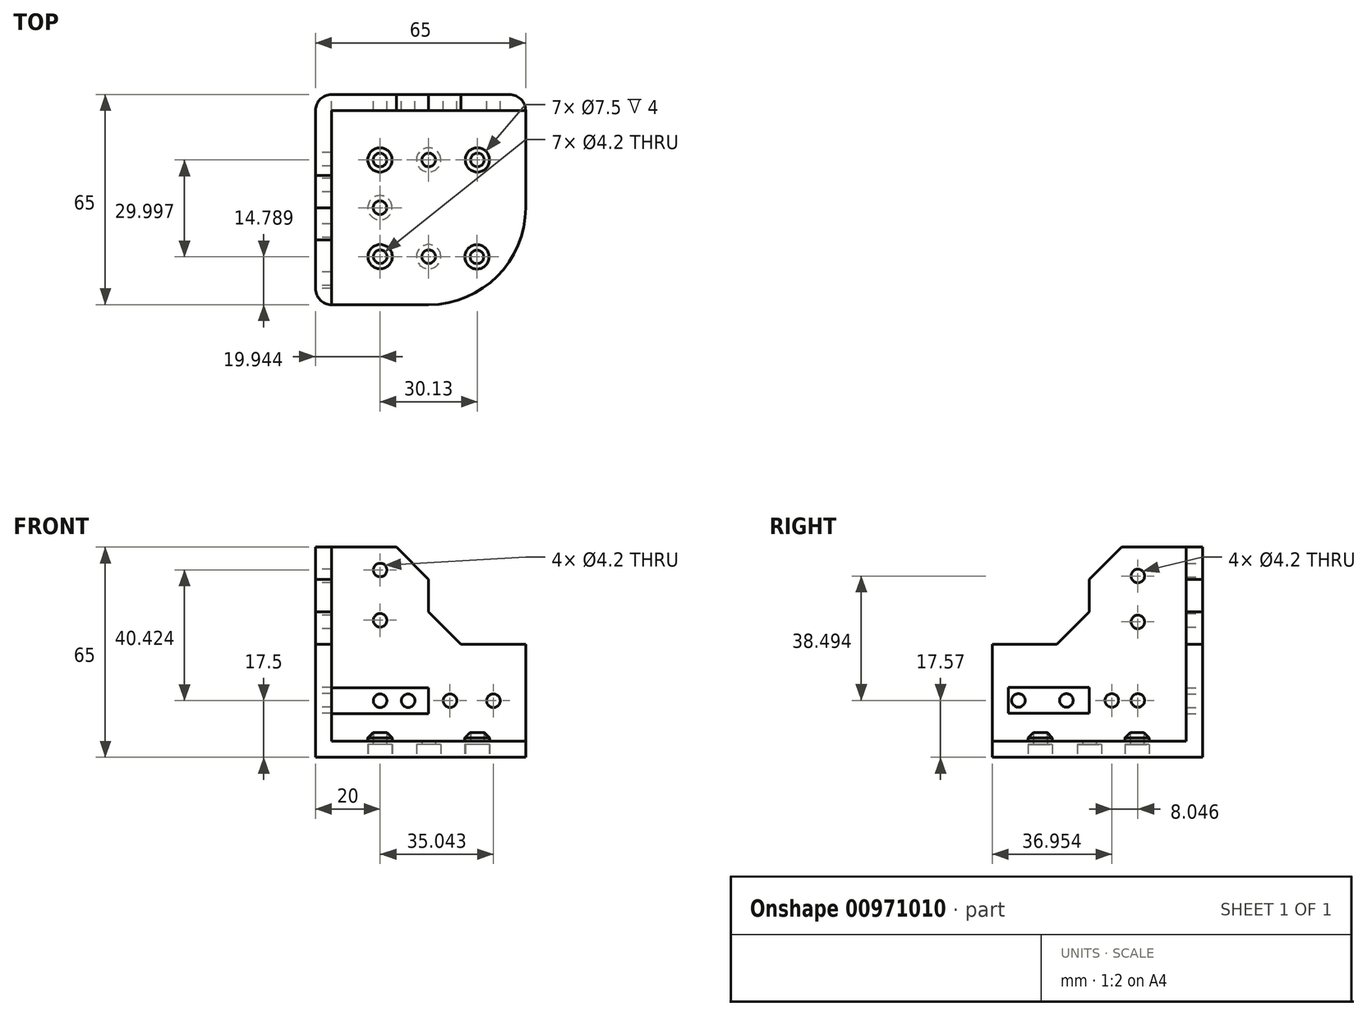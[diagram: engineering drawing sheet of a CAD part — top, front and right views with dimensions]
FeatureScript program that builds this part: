
annotation { "Feature Type Name" : "Feature", "Feature Type Description" : "" }
export const myFeature = defineFeature(function(context is Context, id is Id, definition is map)
    precondition{}
    {
        {
            var Q0;
            Q0=qCreatedBy(makeId("Top.planeOp"),FACE);
            var sketch = newSketch(context, id + "F0", { "sketchPlane" : qUnion([Q0])});
            skLineSegment(sketch, "E0.bottom", {"start": v(0, 0) * mm, "end": v(-30, 0) * mm});
            skLineSegment(sketch, "E0.top", {"start": v(0, 30) * mm, "end": v(-30, 30) * mm});
            skLineSegment(sketch, "E0.left", {"start": v(0, 0) * mm, "end": v(0, 30) * mm});
            skLineSegment(sketch, "E0.right", {"start": v(-30, 0) * mm, "end": v(-30, 30) * mm});
            skLineSegment(sketch, "E1.bottom", {"start": v(0, 30) * mm, "end": v(30, 30) * mm});
            skLineSegment(sketch, "E1.top", {"start": v(0, 0) * mm, "end": v(30, 0) * mm});
            skLineSegment(sketch, "E1.left", {"start": v(0, 30) * mm, "end": v(0, 0) * mm});
            skLineSegment(sketch, "E1.right", {"start": v(30, 30) * mm, "end": v(30, 0) * mm});
            skLineSegment(sketch, "E2.top", {"start": v(0, -30) * mm, "end": v(-30, -30) * mm});
            skLineSegment(sketch, "E2.left", {"start": v(0, 0) * mm, "end": v(0, -30) * mm});
            skLineSegment(sketch, "E2.right", {"start": v(-30, 0) * mm, "end": v(-30, -30) * mm});
            skLineSegment(sketch, "E3.bottom", {"start": v(-30, 30) * mm, "end": v(30, 30) * mm});
            skLineSegment(sketch, "E3.top", {"start": v(-30, 35) * mm, "end": v(25, 35) * mm});
            skLineSegment(sketch, "E3.left", {"start": v(-30, 30) * mm, "end": v(-30, 35) * mm});
            skLineSegment(sketch, "E3.right", {"start": v(30, 30) * mm, "end": v(30, 30) * mm});
            skLineSegment(sketch, "E4.bottom", {"start": v(-30, 30) * mm, "end": v(-35, 30) * mm});
            skLineSegment(sketch, "E4.top", {"start": v(-30, -30) * mm, "end": v(-30, -30) * mm});
            skLineSegment(sketch, "E4.left", {"start": v(-30, 30) * mm, "end": v(-30, -30) * mm});
            skLineSegment(sketch, "E4.right", {"start": v(-35, 30) * mm, "end": v(-35, -25) * mm});
            skLineSegment(sketch, "E5.top", {"start": v(-30, 35) * mm, "end": v(-30, 35) * mm});
            skLineSegment(sketch, "E5.right", {"start": v(-35, 30) * mm, "end": v(-35, 30) * mm});
            skArc(sketch, "E6", {"start": v(0, -30) * mm, "mid": v(21.21, -21.21) * mm, "end": v(30, 0) * mm});
            skPoint(sketch, "E7.visualSharp", {"position": v(-35, 35) * mm});
            skArc(sketch, "E7.filletArc", {"start": v(-30, 35) * mm, "mid": v(-33.54, 33.54) * mm, "end": v(-35, 30) * mm});
            skPoint(sketch, "E8.visualSharp", {"position": v(30, 35) * mm});
            skArc(sketch, "E8.filletArc", {"start": v(30, 30) * mm, "mid": v(28.54, 33.54) * mm, "end": v(25, 35) * mm});
            skPoint(sketch, "E9.visualSharp", {"position": v(-35, -30) * mm});
            skArc(sketch, "E9.filletArc", {"start": v(-35, -25) * mm, "mid": v(-33.54, -28.54) * mm, "end": v(-30, -30) * mm});
            skLineSegment(sketch, "E10", {"start": v(0, 30) * mm, "end": v(0, 35) * mm});
            skLineSegment(sketch, "E11", {"start": v(-30, 0) * mm, "end": v(-35, 0) * mm});
            skSolve(sketch);
        }
        {
            var Q0;
            {var subQ0=makeQuery(id+"F0.imprint","IMPRINT",EDGE,{"derivedFrom":sQuery(id+"F0.wireOp",EDGE,"E2.right")});var subQ7=sQuery(id+"F0.wireOp",EDGE,"E3.left");var subQ12=makeQuery(id+"F0.imprint","IMPRINT",EDGE,{"derivedFrom":subQ7});var subQ13=makeQuery(id+"F0.imprint","IMPRINT",EDGE,{"derivedFrom":sQuery(id+"F0.wireOp",EDGE,"E1.top")});var subQ17=makeQuery(id+"F0.imprint","IMPRINT",EDGE,{"derivedFrom":sQuery(id+"F0.wireOp",EDGE,"E1.bottom")});Q0=qUnion([makeQuery(id+"F0.imprint","IMPRINT",FACE,{"disambiguationData":[TD([[subQ12,1.0]])]}),makeQuery(id+"F0.imprint","IMPRINT",FACE,{"disambiguationData":[TD([[makeQuery(id+"F0.imprint","IMPRINT",EDGE,{"derivedFrom":sQuery(id+"F0.wireOp",EDGE,"E0.left")}),-1.0]])]}),makeQuery(id+"F0.imprint","IMPRINT",FACE,{"disambiguationData":[TD([[subQ17,1.0]])]}),makeQuery(id+"F0.imprint","IMPRINT",FACE,{"disambiguationData":[TD([[makeQuery(id+"F0.imprint","IMPRINT",EDGE,{"derivedFrom":sQuery(id+"F0.wireOp",EDGE,"E0.bottom")}),1.0]])]}),makeQuery(id+"F0.imprint","IMPRINT",FACE,{"disambiguationData":[TD([[makeQuery(id+"F0.imprint","IMPRINT",EDGE,{"derivedFrom":sQuery(id+"F0.wireOp",EDGE,"E0.right")}),1.0]])]}),makeQuery(id+"F0.imprint","IMPRINT",FACE,{"disambiguationData":[TD([[subQ13,-1.0]])]}),makeQuery(id+"F0.imprint","IMPRINT",FACE,{"disambiguationData":[TD([[makeQuery(id+"F0.imprint","IMPRINT",EDGE,{"derivedFrom":sQuery(id+"F0.wireOp",EDGE,"E0.top")}),-1.0]])]}),makeQuery(id+"F0.imprint","IMPRINT",FACE,{"disambiguationData":[TD([[subQ0,-1.0]])]})]);}
            var Q1;
            Q1=makeQuery(id+"F0.imprint","IMPRINT",FACE,{"disambiguationData":[TD([[makeQuery(id+"F0.imprint","IMPRINT",EDGE,{"derivedFrom":sQuery(id+"F0.wireOp",EDGE,"E0.bottom")}),-1.0]])]});
            extrude(context, id + "F1", {"entities" : qUnion([Q0, Q1]), "depth" : 5 * mm, "offsetDistance" : 25 * mm});
        }
        {
            var Q0;
            {Q0=qUnion([makeQuery(id+"F0.imprint","IMPRINT",FACE,{"disambiguationData":[TD([[makeQuery(id+"F0.imprint","IMPRINT",EDGE,{"derivedFrom":sQuery(id+"F0.wireOp",EDGE,"E2.right")}),-1.0]])]}),makeQuery(id+"F0.imprint","IMPRINT",FACE,{"disambiguationData":[TD([[makeQuery(id+"F0.imprint","IMPRINT",EDGE,{"derivedFrom":sQuery(id+"F0.wireOp",EDGE,"E0.right")}),1.0]])]})]);}
            var Q1;
            Q1=makeQuery(id+"F0.imprint","IMPRINT",FACE,{"disambiguationData":[TD([[makeQuery(id+"F0.imprint","IMPRINT",EDGE,{"derivedFrom":sQuery(id+"F0.wireOp",EDGE,"E3.left")}),1.0]])]});
            var Q2;
            {Q2=qUnion([makeQuery(id+"F0.imprint","IMPRINT",FACE,{"disambiguationData":[TD([[makeQuery(id+"F0.imprint","IMPRINT",EDGE,{"derivedFrom":sQuery(id+"F0.wireOp",EDGE,"E1.bottom")}),1.0]])]}),makeQuery(id+"F0.imprint","IMPRINT",FACE,{"disambiguationData":[TD([[makeQuery(id+"F0.imprint","IMPRINT",EDGE,{"derivedFrom":sQuery(id+"F0.wireOp",EDGE,"E0.top")}),-1.0]])]})]);}
            extrude(context, id + "F2", {"entities" : qUnion([Q0, Q1, Q2]), "operationType" : NewBodyOperationType.ADD, "depth" : 35 * mm, "offsetDistance" : 25 * mm});
        }
        {
            var Q0;
            Q0=makeQuery(id+"F0.imprint","IMPRINT",FACE,{"disambiguationData":[TD([[makeQuery(id+"F0.imprint","IMPRINT",EDGE,{"derivedFrom":sQuery(id+"F0.wireOp",EDGE,"E0.top")}),-1.0]])]});
            var Q1;
            Q1=makeQuery(id+"F0.imprint","IMPRINT",FACE,{"disambiguationData":[TD([[makeQuery(id+"F0.imprint","IMPRINT",EDGE,{"derivedFrom":sQuery(id+"F0.wireOp",EDGE,"E3.left")}),1.0]])]});
            var Q2;
            Q2=makeQuery(id+"F0.imprint","IMPRINT",FACE,{"disambiguationData":[TD([[makeQuery(id+"F0.imprint","IMPRINT",EDGE,{"derivedFrom":sQuery(id+"F0.wireOp",EDGE,"E0.right")}),1.0]])]});
            extrude(context, id + "F3", {"entities" : qUnion([Q0, Q1, Q2]), "operationType" : NewBodyOperationType.ADD, "depth" : 65 * mm, "offsetDistance" : 25 * mm});
        }
        {
            var Q0;
            {var subQ0=sQuery(id+"F0.wireOp",EDGE,"E3.top");Q0=makeQuery(id+"F3.boolean.opBoolean","MERGE",FACE,{"derivedFrom":[makeQuery(id+"F2.boolean.opBoolean","MERGE",FACE,{"derivedFrom":[makeQuery(id+"F1.opExtrude","SWEPT_FACE",FACE,{"disambiguationData":[OSD([subQ0])]}),makeQuery(id+"F2.opExtrude","SWEPT_FACE",FACE,{"disambiguationData":[OSD([subQ0])]})]}),makeQuery(id+"F3.opExtrude","SWEPT_FACE",FACE,{"disambiguationData":[OSD([subQ0])]})]});}
            var sketch = newSketch(context, id + "F4", { "sketchPlane" : qUnion([Q0])});
            skLineSegment(sketch, "E12.bottom", {"start": v(-25, 0) * mm, "end": v(30, 0) * mm, "construction": true});
            skLineSegment(sketch, "E12.top", {"start": v(-25, 35) * mm, "end": v(30, 35) * mm, "construction": true});
            skLineSegment(sketch, "E12.left", {"start": v(-25, 0) * mm, "end": v(-25, 35) * mm, "construction": true});
            skLineSegment(sketch, "E12.right", {"start": v(30, 0) * mm, "end": v(30, 35) * mm, "construction": true});
            skLineSegment(sketch, "E13.bottom", {"start": v(-25, 21.5) * mm, "end": v(30, 21.5) * mm});
            skLineSegment(sketch, "E13.top", {"start": v(-25, 13.5) * mm, "end": v(30, 13.5) * mm});
            skLineSegment(sketch, "E13.left", {"start": v(-25, 21.5) * mm, "end": v(-25, 13.5) * mm});
            skLineSegment(sketch, "E13.right", {"start": v(30, 21.5) * mm, "end": v(30, 13.5) * mm});
            skLineSegment(sketch, "E14", {"start": v(0, 21.5) * mm, "end": v(0, 13.5) * mm});
            skCircle(sketch, "E15", {"center": v(-20.04, 17.5) * mm, "radius": 2.1 * mm});
            skPoint(sketch, "E15.centerSnap0", {"position": v(-25, 17.5) * mm});
            skCircle(sketch, "E16", {"center": v(-6.61, 17.5) * mm, "radius": 2.1 * mm});
            skCircle(sketch, "E17.MirrorC", {"center": v(15, 17.5) * mm, "radius": 2.1 * mm});
            skCircle(sketch, "E18.MirrorC", {"center": v(6.32, 17.5) * mm, "radius": 2.1 * mm});
            skCircle(sketch, "E19", {"center": v(15, 57.92) * mm, "radius": 2.1 * mm});
            skCircle(sketch, "E20", {"center": v(15, 42.38) * mm, "radius": 2.1 * mm});
            skSolve(sketch);
        }
        {
            var Q0;
            {var subQ0=sQuery(id+"F0.wireOp",EDGE,"E4.right");Q0=makeQuery(id+"F3.boolean.opBoolean","MERGE",FACE,{"derivedFrom":[makeQuery(id+"F2.boolean.opBoolean","MERGE",FACE,{"derivedFrom":[makeQuery(id+"F1.opExtrude","SWEPT_FACE",FACE,{"disambiguationData":[OSD([subQ0])]}),makeQuery(id+"F2.opExtrude","SWEPT_FACE",FACE,{"disambiguationData":[OSD([subQ0])]})]}),makeQuery(id+"F3.opExtrude","SWEPT_FACE",FACE,{"disambiguationData":[OSD([subQ0])]})]});}
            var sketch = newSketch(context, id + "F5", { "sketchPlane" : qUnion([Q0])});
            skLineSegment(sketch, "E21.bottom", {"start": v(-35, 21.57) * mm, "end": v(25, 21.57) * mm});
            skLineSegment(sketch, "E21.top", {"start": v(-35, 13.57) * mm, "end": v(25, 13.57) * mm});
            skLineSegment(sketch, "E21.left", {"start": v(-35, 21.57) * mm, "end": v(-35, 13.57) * mm});
            skLineSegment(sketch, "E21.right", {"start": v(25, 21.57) * mm, "end": v(25, 13.57) * mm});
            skLineSegment(sketch, "E22", {"start": v(0, 21.57) * mm, "end": v(0, 13.57) * mm});
            skCircle(sketch, "E23", {"center": v(-6.95, 17.57) * mm, "radius": 2.1 * mm});
            skPoint(sketch, "E23.centerSnap0", {"position": v(-35, 17.57) * mm});
            skCircle(sketch, "E24", {"center": v(-15, 17.57) * mm, "radius": 2.1 * mm});
            skCircle(sketch, "E25.MirrorC", {"center": v(7.1, 17.57) * mm, "radius": 2.1 * mm});
            skCircle(sketch, "E26.MirrorC", {"center": v(21.94, 17.57) * mm, "radius": 2.1 * mm});
            skCircle(sketch, "E27", {"center": v(-15, 41.87) * mm, "radius": 2.1 * mm});
            skCircle(sketch, "E28", {"center": v(-15, 56.06) * mm, "radius": 2.1 * mm});
            skSolve(sketch);
        }
        {
            var Q0;
            Q0=makeQuery(id+"F4.imprint","IMPRINT",FACE,{"disambiguationData":[TD([[makeQuery(id+"F4.imprint","IMPRINT",EDGE,{"derivedFrom":sQuery(id+"F4.wireOp",EDGE,"E17.MirrorC")}),-1.0]])]});
            var Q1;
            Q1=makeQuery(id+"F4.imprint","IMPRINT",FACE,{"disambiguationData":[TD([[makeQuery(id+"F4.imprint","IMPRINT",EDGE,{"derivedFrom":sQuery(id+"F4.wireOp",EDGE,"E18.MirrorC")}),-1.0]])]});
            var Q2;
            Q2=makeQuery(id+"F4.imprint","IMPRINT",FACE,{"disambiguationData":[TD([[makeQuery(id+"F4.imprint","IMPRINT",EDGE,{"derivedFrom":sQuery(id+"F4.wireOp",EDGE,"E16")}),1.0]])]});
            var Q3;
            Q3=makeQuery(id+"F4.imprint","IMPRINT",FACE,{"disambiguationData":[TD([[makeQuery(id+"F4.imprint","IMPRINT",EDGE,{"derivedFrom":sQuery(id+"F4.wireOp",EDGE,"E15")}),1.0]])]});
            var Q4;
            Q4=makeQuery(id+"F4.imprint","IMPRINT",FACE,{"disambiguationData":[TD([[makeQuery(id+"F4.imprint","IMPRINT",EDGE,{"derivedFrom":sQuery(id+"F4.wireOp",EDGE,"E20")}),1.0]])]});
            var Q5;
            Q5=makeQuery(id+"F4.imprint","IMPRINT",FACE,{"disambiguationData":[TD([[makeQuery(id+"F4.imprint","IMPRINT",EDGE,{"derivedFrom":sQuery(id+"F4.wireOp",EDGE,"E19")}),1.0]])]});
            extrude(context, id + "F6", {"entities" : qUnion([Q0, Q1, Q2, Q3, Q4, Q5]), "operationType" : NewBodyOperationType.REMOVE, "oppositeDirection" : true, "depth" : 25 * mm, "offsetDistance" : 25 * mm});
        }
        {
            var Q0;
            Q0=makeQuery(id+"F5.imprint","IMPRINT",FACE,{"disambiguationData":[TD([[makeQuery(id+"F5.imprint","IMPRINT",EDGE,{"derivedFrom":sQuery(id+"F5.wireOp",EDGE,"E26.MirrorC")}),-1.0]])]});
            var Q1;
            Q1=makeQuery(id+"F5.imprint","IMPRINT",FACE,{"disambiguationData":[TD([[makeQuery(id+"F5.imprint","IMPRINT",EDGE,{"derivedFrom":sQuery(id+"F5.wireOp",EDGE,"E25.MirrorC")}),-1.0]])]});
            var Q2;
            Q2=makeQuery(id+"F5.imprint","IMPRINT",FACE,{"disambiguationData":[TD([[makeQuery(id+"F5.imprint","IMPRINT",EDGE,{"derivedFrom":sQuery(id+"F5.wireOp",EDGE,"E24")}),1.0]])]});
            var Q3;
            Q3=makeQuery(id+"F5.imprint","IMPRINT",FACE,{"disambiguationData":[TD([[makeQuery(id+"F5.imprint","IMPRINT",EDGE,{"derivedFrom":sQuery(id+"F5.wireOp",EDGE,"E23")}),1.0]])]});
            var Q4;
            Q4=makeQuery(id+"F5.imprint","IMPRINT",FACE,{"disambiguationData":[TD([[makeQuery(id+"F5.imprint","IMPRINT",EDGE,{"derivedFrom":sQuery(id+"F5.wireOp",EDGE,"E27")}),1.0]])]});
            var Q5;
            Q5=makeQuery(id+"F5.imprint","IMPRINT",FACE,{"disambiguationData":[TD([[makeQuery(id+"F5.imprint","IMPRINT",EDGE,{"derivedFrom":sQuery(id+"F5.wireOp",EDGE,"E28")}),1.0]])]});
            extrude(context, id + "F7", {"entities" : qUnion([Q0, Q1, Q2, Q3, Q4, Q5]), "operationType" : NewBodyOperationType.REMOVE, "oppositeDirection" : true, "depth" : 25 * mm, "offsetDistance" : 25 * mm});
        }
        {
            var Q0;
            Q0=makeQuery(id+"F0.imprint","IMPRINT",FACE,{"disambiguationData":[TD([[makeQuery(id+"F0.imprint","IMPRINT",EDGE,{"derivedFrom":sQuery(id+"F0.wireOp",EDGE,"E0.bottom")}),1.0]])]});
            var sketch = newSketch(context, id + "F8", { "sketchPlane" : qUnion([Q0])});
            skLineSegment(sketch, "E29", {"start": v(-30.14, -30.28) * mm, "end": v(30.02, 29.68) * mm, "construction": true});
            skLineSegment(sketch, "E30", {"start": v(30.02, 29.68) * mm, "end": v(-29.98, 29.68) * mm, "construction": true});
            skLineSegment(sketch, "E31", {"start": v(-29.98, 29.68) * mm, "end": v(30.02, -30.28) * mm, "construction": true});
            skLineSegment(sketch, "E32", {"start": v(30.02, -30.28) * mm, "end": v(-30.14, -30.28) * mm, "construction": true});
            skLineSegment(sketch, "E33", {"start": v(0.02, 29.68) * mm, "end": v(-29.98, 0) * mm, "construction": true});
            skLineSegment(sketch, "E34", {"start": v(-29.98, 0) * mm, "end": v(30.02, 0) * mm, "construction": true});
            skLineSegment(sketch, "E35", {"start": v(30.02, 0) * mm, "end": v(0.02, 29.68) * mm, "construction": true});
            skLineSegment(sketch, "E36", {"start": v(0, -30.28) * mm, "end": v(-29.98, 0) * mm, "construction": true});
            skLineSegment(sketch, "E37", {"start": v(0, -30.28) * mm, "end": v(30.02, 0) * mm, "construction": true});
            skCircle(sketch, "E38", {"center": v(15.07, 14.79) * mm, "radius": 2.1 * mm});
            skCircle(sketch, "E39", {"center": v(-15, -15.14) * mm, "radius": 2.1 * mm});
            skCircle(sketch, "E40", {"center": v(-15.06, 14.77) * mm, "radius": 2.1 * mm});
            skCircle(sketch, "E41", {"center": v(0, 14.77) * mm, "radius": 2.1 * mm});
            skCircle(sketch, "E42", {"center": v(-15.06, 0) * mm, "radius": 2.1 * mm});
            skCircle(sketch, "E43", {"center": v(0, -15.14) * mm, "radius": 2.1 * mm});
            skCircle(sketch, "E44", {"center": v(14.94, -15.21) * mm, "radius": 2.1 * mm});
            skCircle(sketch, "E45", {"center": v(-15.06, 14.77) * mm, "radius": 3.75 * mm});
            skCircle(sketch, "E46", {"center": v(0, 14.77) * mm, "radius": 3.75 * mm});
            skCircle(sketch, "E47", {"center": v(15.07, 14.79) * mm, "radius": 3.75 * mm});
            skCircle(sketch, "E48", {"center": v(14.94, -15.21) * mm, "radius": 3.75 * mm});
            skCircle(sketch, "E49", {"center": v(0, -15.14) * mm, "radius": 3.75 * mm});
            skCircle(sketch, "E50", {"center": v(-15, -15.14) * mm, "radius": 3.75 * mm});
            skCircle(sketch, "E51", {"center": v(-15.06, 0) * mm, "radius": 3.75 * mm});
            skSolve(sketch);
        }
        {
            var Q0;
            Q0 = qSketchRegion(id + "F8", true);
            extrude(context, id + "F9", {"entities" : qUnion([Q0]), "operationType" : NewBodyOperationType.REMOVE, "depth" : 4 * mm, "offsetDistance" : 25 * mm});
        }
        {
            var Q0;
            Q0=makeQuery(id+"F8.imprint","IMPRINT",FACE,{"disambiguationData":[TD([[makeQuery(id+"F8.imprint","IMPRINT",EDGE,{"derivedFrom":sQuery(id+"F8.wireOp",EDGE,"E39")}),1.0]])]});
            var Q1;
            {var subQ0=sQuery(id+"F8.wireOp",EDGE,"E43");var subQ1=makeQuery(id+"F0.imprint","IMPRINT",EDGE,{"derivedFrom":sQuery(id+"F0.wireOp",EDGE,"E2.left")});var subQ2=makeQuery(id+"F8.imprint","INTERSECT",VERTEX,{"disambiguationData":[OD(0.0)],"derivedFrom":[subQ1,subQ0]});Q1=makeQuery(id+"F8.imprint","IMPRINT",FACE,{"disambiguationData":[TD([[makeQuery(id+"F8.imprint","IMPRINT",EDGE,{"disambiguationData":[TD([[subQ2,-1.0]])],"derivedFrom":subQ0}),1.0]])]});}
            var Q2;
            {var subQ0=sQuery(id+"F8.wireOp",EDGE,"E43");var subQ1=makeQuery(id+"F0.imprint","IMPRINT",EDGE,{"derivedFrom":sQuery(id+"F0.wireOp",EDGE,"E2.left")});var subQ2=makeQuery(id+"F8.imprint","INTERSECT",VERTEX,{"disambiguationData":[OD(0.0)],"derivedFrom":[subQ1,subQ0]});Q2=makeQuery(id+"F8.imprint","IMPRINT",FACE,{"disambiguationData":[TD([[makeQuery(id+"F8.imprint","IMPRINT",EDGE,{"disambiguationData":[TD([[subQ2,1.0]])],"derivedFrom":subQ0}),1.0]])]});}
            var Q3;
            Q3=makeQuery(id+"F8.imprint","IMPRINT",FACE,{"disambiguationData":[TD([[makeQuery(id+"F8.imprint","IMPRINT",EDGE,{"derivedFrom":sQuery(id+"F8.wireOp",EDGE,"E44")}),1.0]])]});
            var Q4;
            Q4=makeQuery(id+"F8.imprint","IMPRINT",FACE,{"disambiguationData":[TD([[makeQuery(id+"F8.imprint","IMPRINT",EDGE,{"derivedFrom":sQuery(id+"F8.wireOp",EDGE,"E38")}),1.0]])]});
            var Q5;
            Q5=makeQuery(id+"F8.imprint","IMPRINT",FACE,{"disambiguationData":[TD([[makeQuery(id+"F8.imprint","IMPRINT",EDGE,{"derivedFrom":sQuery(id+"F8.wireOp",EDGE,"E41")}),1.0]])]});
            var Q6;
            Q6=makeQuery(id+"F8.imprint","IMPRINT",FACE,{"disambiguationData":[TD([[makeQuery(id+"F8.imprint","IMPRINT",EDGE,{"derivedFrom":sQuery(id+"F8.wireOp",EDGE,"E40")}),1.0]])]});
            var Q7;
            {var subQ0=sQuery(id+"F8.wireOp",EDGE,"E42");var subQ1=makeQuery(id+"F0.imprint","IMPRINT",EDGE,{"derivedFrom":sQuery(id+"F0.wireOp",EDGE,"E0.bottom")});var subQ2=makeQuery(id+"F8.imprint","INTERSECT",VERTEX,{"disambiguationData":[OD(0.0)],"derivedFrom":[subQ1,subQ0]});Q7=makeQuery(id+"F8.imprint","IMPRINT",FACE,{"disambiguationData":[TD([[makeQuery(id+"F8.imprint","IMPRINT",EDGE,{"disambiguationData":[TD([[subQ2,-1.0]])],"derivedFrom":subQ0}),1.0]])]});}
            var Q8;
            {var subQ0=sQuery(id+"F8.wireOp",EDGE,"E42");var subQ1=makeQuery(id+"F0.imprint","IMPRINT",EDGE,{"derivedFrom":sQuery(id+"F0.wireOp",EDGE,"E0.bottom")});var subQ2=makeQuery(id+"F8.imprint","INTERSECT",VERTEX,{"disambiguationData":[OD(0.0)],"derivedFrom":[subQ1,subQ0]});Q8=makeQuery(id+"F8.imprint","IMPRINT",FACE,{"disambiguationData":[TD([[makeQuery(id+"F8.imprint","IMPRINT",EDGE,{"disambiguationData":[TD([[subQ2,1.0]])],"derivedFrom":subQ0}),1.0]])]});}
            extrude(context, id + "F10", {"entities" : qUnion([Q0, Q1, Q2, Q3, Q4, Q5, Q6, Q7, Q8]), "operationType" : NewBodyOperationType.REMOVE, "depth" : 25 * mm, "offsetDistance" : 25 * mm});
        }
        {
            var Q0;
            Q0=makeQuery(id+"F8.imprint","IMPRINT",FACE,{"disambiguationData":[TD([[makeQuery(id+"F8.imprint","IMPRINT",EDGE,{"derivedFrom":sQuery(id+"F8.wireOp",EDGE,"E39")}),-1.0]])]});
            var Q1;
            Q1=makeQuery(id+"F8.imprint","IMPRINT",FACE,{"disambiguationData":[TD([[makeQuery(id+"F8.imprint","IMPRINT",EDGE,{"derivedFrom":sQuery(id+"F8.wireOp",EDGE,"E44")}),-1.0]])]});
            var Q2;
            Q2=makeQuery(id+"F8.imprint","IMPRINT",FACE,{"disambiguationData":[TD([[makeQuery(id+"F8.imprint","IMPRINT",EDGE,{"derivedFrom":sQuery(id+"F8.wireOp",EDGE,"E40")}),-1.0]])]});
            var Q3;
            Q3=makeQuery(id+"F8.imprint","IMPRINT",FACE,{"disambiguationData":[TD([[makeQuery(id+"F8.imprint","IMPRINT",EDGE,{"derivedFrom":sQuery(id+"F8.wireOp",EDGE,"E38")}),-1.0]])]});
            extrude(context, id + "F11", {"entities" : qUnion([Q0, Q1, Q2, Q3]), "operationType" : NewBodyOperationType.ADD, "depth" : 8 * mm, "offsetDistance" : 25 * mm, "hasSecondDirection" : true, "secondDirectionOppositeDirection" : false, "secondDirectionDepth" : 4 * mm});
        }
        {
            var Q0;
            Q0=makeQuery(id+"F11.opExtrude","CAP_EDGE",EDGE,{"disambiguationData":[OSD([sQuery(id+"F8.wireOp",EDGE,"E45")])],"isStart":false});
            var Q1;
            Q1=makeQuery(id+"F11.opExtrude","CAP_EDGE",EDGE,{"disambiguationData":[OSD([sQuery(id+"F8.wireOp",EDGE,"E46")])],"isStart":false});
            var Q2;
            Q2=makeQuery(id+"F11.opExtrude","CAP_EDGE",EDGE,{"disambiguationData":[OSD([sQuery(id+"F8.wireOp",EDGE,"E47")])],"isStart":false});
            var Q3;
            Q3=makeQuery(id+"F11.opExtrude","CAP_EDGE",EDGE,{"disambiguationData":[OSD([sQuery(id+"F8.wireOp",EDGE,"E48")])],"isStart":false});
            var Q4;
            Q4=makeQuery(id+"F11.opExtrude","CAP_EDGE",EDGE,{"disambiguationData":[OSD([sQuery(id+"F8.wireOp",EDGE,"E49")])],"isStart":false});
            var Q5;
            Q5=makeQuery(id+"F11.opExtrude","CAP_EDGE",EDGE,{"disambiguationData":[OSD([sQuery(id+"F8.wireOp",EDGE,"E50")])],"isStart":false});
            chamfer(context, id + "F12", {"entities" : qUnion([Q0, Q1, Q2, Q3, Q4, Q5]), "width" : 2 * mm, "tangentPropagation" : true});
        }
        {
            var Q0;
            Q0=makeQuery(id+"F3.opExtrude","CAP_EDGE",EDGE,{"disambiguationData":[OSD([sQuery(id+"F0.wireOp",EDGE,"E11")])],"isStart":false});
            var Q1;
            Q1=makeQuery(id+"F3.opExtrude","CAP_EDGE",EDGE,{"disambiguationData":[OSD([sQuery(id+"F0.wireOp",EDGE,"E10")])],"isStart":false});
            var Q2;
            Q2=makeQuery(id+"F3.boolean.opBoolean","INTERSECT",EDGE,{"derivedFrom":[makeQuery(id+"F2.opExtrude","CAP_FACE",FACE,{"disambiguationData":[OSD([sQuery(id+"F0.wireOp",EDGE,"E0.top"),sQuery(id+"F0.wireOp",EDGE,"E0.right"),sQuery(id+"F0.wireOp",EDGE,"E1.bottom"),sQuery(id+"F0.wireOp",EDGE,"E2.right"),sQuery(id+"F0.wireOp",EDGE,"E3.top"),sQuery(id+"F0.wireOp",EDGE,"E4.right"),sQuery(id+"F0.wireOp",EDGE,"E7.filletArc"),sQuery(id+"F0.wireOp",EDGE,"E8.filletArc"),sQuery(id+"F0.wireOp",EDGE,"E9.filletArc")])],"isStart":false}),makeQuery(id+"F3.opExtrude","SWEPT_FACE",FACE,{"disambiguationData":[OSD([sQuery(id+"F0.wireOp",EDGE,"E11")])]})]});
            var Q3;
            Q3=makeQuery(id+"F3.boolean.opBoolean","INTERSECT",EDGE,{"derivedFrom":[makeQuery(id+"F2.opExtrude","CAP_FACE",FACE,{"disambiguationData":[OSD([sQuery(id+"F0.wireOp",EDGE,"E0.top"),sQuery(id+"F0.wireOp",EDGE,"E0.right"),sQuery(id+"F0.wireOp",EDGE,"E1.bottom"),sQuery(id+"F0.wireOp",EDGE,"E2.right"),sQuery(id+"F0.wireOp",EDGE,"E3.top"),sQuery(id+"F0.wireOp",EDGE,"E4.right"),sQuery(id+"F0.wireOp",EDGE,"E7.filletArc"),sQuery(id+"F0.wireOp",EDGE,"E8.filletArc"),sQuery(id+"F0.wireOp",EDGE,"E9.filletArc")])],"isStart":false}),makeQuery(id+"F3.opExtrude","SWEPT_FACE",FACE,{"disambiguationData":[OSD([sQuery(id+"F0.wireOp",EDGE,"E10")])]})]});
            chamfer(context, id + "F13", {"entities" : qUnion([Q0, Q1, Q2, Q3]), "width" : 10 * mm, "tangentPropagation" : true});
        }
    });
